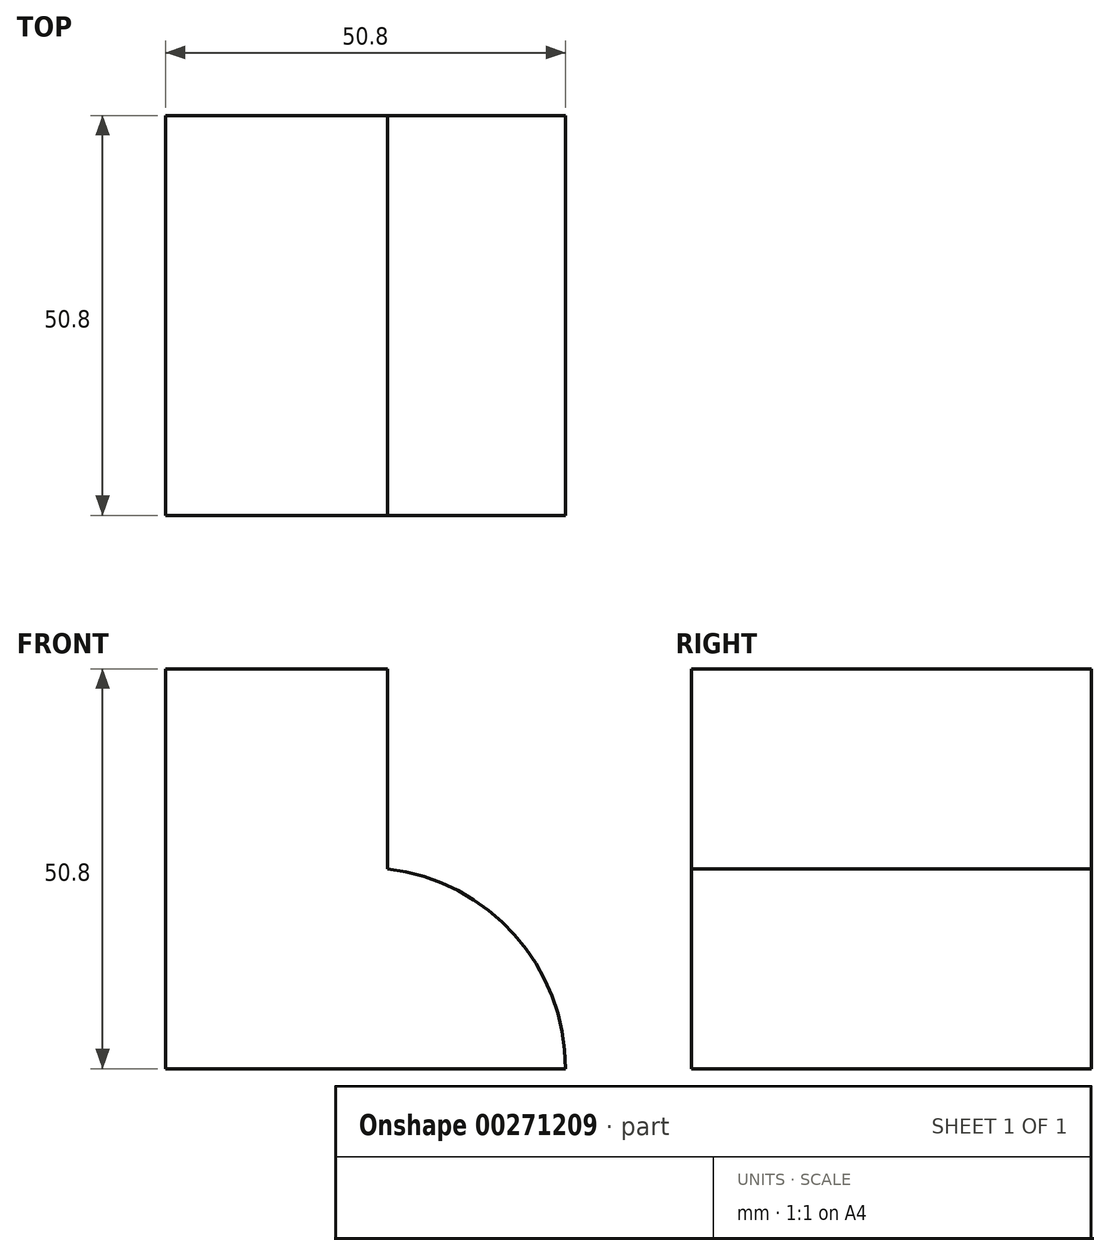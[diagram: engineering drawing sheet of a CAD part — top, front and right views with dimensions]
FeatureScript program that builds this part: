
annotation { "Feature Type Name" : "Feature", "Feature Type Description" : "" }
export const myFeature = defineFeature(function(context is Context, id is Id, definition is map)
    precondition{}
    {
        {
            var Q0;
            Q0=qCreatedBy(makeId("Front.planeOp"),FACE);
            var sketch = newSketch(context, id + "F0", { "sketchPlane" : qUnion([Q0])});
            skLineSegment(sketch, "E0.bottom", {"start": v(0, 0) * mm, "end": v(-50.8, 0) * mm});
            skLineSegment(sketch, "E0.top", {"start": v(0, 50.8) * mm, "end": v(-50.8, 50.8) * mm});
            skLineSegment(sketch, "E0.left", {"start": v(0, 0) * mm, "end": v(0, 50.8) * mm});
            skLineSegment(sketch, "E0.right", {"start": v(-50.8, 0) * mm, "end": v(-50.8, 50.8) * mm});
            skSolve(sketch);
        }
        {
            var Q0;
            Q0 = qSketchRegion(id + "F0", true);
            extrude(context, id + "F1", {"entities" : qUnion([Q0]), "depth" : 50.8 * mm});
        }
        {
            var Q0;
            Q0=makeQuery(id+"F1.opExtrude","CAP_FACE",FACE,{"disambiguationData":[OSD([sQuery(id+"F0.wireOp",EDGE,"E0.bottom"),sQuery(id+"F0.wireOp",EDGE,"E0.top"),sQuery(id+"F0.wireOp",EDGE,"E0.left"),sQuery(id+"F0.wireOp",EDGE,"E0.right")])],"isStart":false});
            var sketch = newSketch(context, id + "F2", { "sketchPlane" : qUnion([Q0])});
            skArc(sketch, "E1", {"start": v(0, 0) * mm, "mid": v(-6.47, 17) * mm, "end": v(-22.62, 25.4) * mm});
            skPoint(sketch, "E1.endSnap0", {"position": v(0, 25.4) * mm});
            skLineSegment(sketch, "E2", {"start": v(-22.62, 25.4) * mm, "end": v(-22.62, 50.8) * mm});
            skPoint(sketch, "E2.endSnap0", {"position": v(-25.4, 50.8) * mm});
            skLineSegment(sketch, "E3", {"start": v(-22.62, 50.8) * mm, "end": v(0, 50.8) * mm});
            skLineSegment(sketch, "E4", {"start": v(0, 50.8) * mm, "end": v(0, 0) * mm});
            skSolve(sketch);
        }
        {
            var Q0;
            Q0 = qSketchRegion(id + "F2", true);
            extrude(context, id + "F3", {"entities" : qUnion([Q0]), "operationType" : NewBodyOperationType.REMOVE, "oppositeDirection" : true, "depth" : 50.8 * mm});
        }
    });
